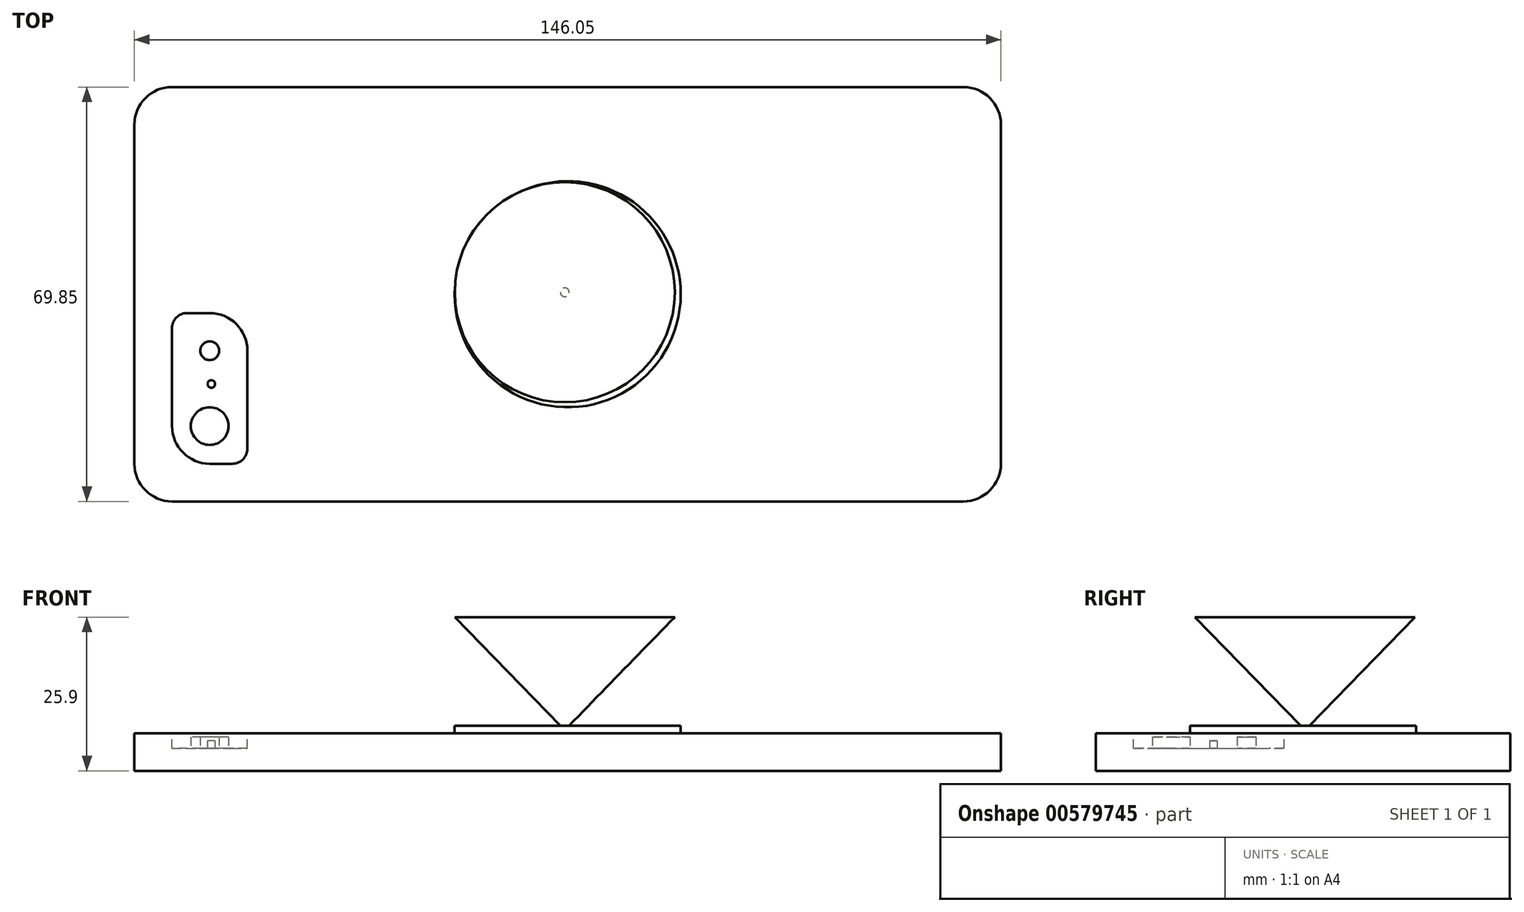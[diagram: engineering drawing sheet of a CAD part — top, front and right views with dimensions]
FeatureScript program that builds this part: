
annotation { "Feature Type Name" : "Feature", "Feature Type Description" : "" }
export const myFeature = defineFeature(function(context is Context, id is Id, definition is map)
    precondition{}
    {
        {
            var Q0;
            Q0=qCreatedBy(makeId("Top.planeOp"),FACE);
            var sketch = newSketch(context, id + "F0", { "sketchPlane" : qUnion([Q0])});
            skLineSegment(sketch, "E0.bottom", {"start": v(-46.88, 61.88) * mm, "end": v(86.47, 61.88) * mm});
            skLineSegment(sketch, "E0.top", {"start": v(-46.88, -7.97) * mm, "end": v(86.47, -7.97) * mm});
            skLineSegment(sketch, "E0.left", {"start": v(-53.23, 55.53) * mm, "end": v(-53.23, -1.62) * mm});
            skLineSegment(sketch, "E0.right", {"start": v(92.82, 55.53) * mm, "end": v(92.82, -1.62) * mm});
            skPoint(sketch, "E1.visualSharp", {"position": v(-53.23, 61.88) * mm});
            skArc(sketch, "E1.filletArc", {"start": v(-46.88, 61.88) * mm, "mid": v(-51.37, 60.02) * mm, "end": v(-53.23, 55.53) * mm});
            skPoint(sketch, "E2.visualSharp", {"position": v(92.82, 61.88) * mm});
            skArc(sketch, "E2.filletArc", {"start": v(92.82, 55.53) * mm, "mid": v(90.96, 60.02) * mm, "end": v(86.47, 61.88) * mm});
            skPoint(sketch, "E3.visualSharp", {"position": v(92.82, -7.97) * mm});
            skArc(sketch, "E3.filletArc", {"start": v(86.47, -7.97) * mm, "mid": v(90.96, -6.1) * mm, "end": v(92.82, -1.62) * mm});
            skPoint(sketch, "E4.visualSharp", {"position": v(-53.23, -7.97) * mm});
            skArc(sketch, "E4.filletArc", {"start": v(-53.23, -1.62) * mm, "mid": v(-51.37, -6.1) * mm, "end": v(-46.88, -7.97) * mm});
            skSolve(sketch);
        }
        {
            var Q0;
            Q0=makeQuery(id+"F0.imprint","IMPRINT",FACE,{"disambiguationData":[TD([[makeQuery(id+"F0.imprint","IMPRINT",EDGE,{"derivedFrom":sQuery(id+"F0.wireOp",EDGE,"E0.bottom")}),-1.0]])]});
            extrude(context, id + "F1", {"entities" : qUnion([Q0]), "depth" : 6.35 * mm, "offsetDistance" : 25.4 * mm});
        }
        {
            var Q0;
            Q0=makeQuery(id+"F1.opExtrude","CAP_FACE",FACE,{"disambiguationData":[OSD([sQuery(id+"F0.wireOp",EDGE,"E0.bottom"),sQuery(id+"F0.wireOp",EDGE,"E0.top"),sQuery(id+"F0.wireOp",EDGE,"E0.left"),sQuery(id+"F0.wireOp",EDGE,"E0.right"),sQuery(id+"F0.wireOp",EDGE,"E1.filletArc"),sQuery(id+"F0.wireOp",EDGE,"E2.filletArc"),sQuery(id+"F0.wireOp",EDGE,"E3.filletArc"),sQuery(id+"F0.wireOp",EDGE,"E4.filletArc")])],"isStart":false});
            var sketch = newSketch(context, id + "F2", { "sketchPlane" : qUnion([Q0])});
            skLineSegment(sketch, "E5.bottom", {"start": v(-40.53, -1.62) * mm, "end": v(-36.72, -1.62) * mm});
            skLineSegment(sketch, "E5.top", {"start": v(-44.34, 23.78) * mm, "end": v(-40.53, 23.78) * mm});
            skLineSegment(sketch, "E5.left", {"start": v(-46.88, 4.73) * mm, "end": v(-46.88, 21.24) * mm});
            skLineSegment(sketch, "E5.right", {"start": v(-34.18, 0.92) * mm, "end": v(-34.18, 17.43) * mm});
            skPoint(sketch, "E6.visualSharp", {"position": v(-46.88, 23.78) * mm});
            skArc(sketch, "E6.filletArc", {"start": v(-44.34, 23.78) * mm, "mid": v(-46.14, 23.04) * mm, "end": v(-46.88, 21.24) * mm});
            skPoint(sketch, "E7.visualSharp", {"position": v(-34.18, -1.62) * mm});
            skArc(sketch, "E7.filletArc", {"start": v(-36.72, -1.62) * mm, "mid": v(-34.93, -0.87) * mm, "end": v(-34.18, 0.92) * mm});
            skPoint(sketch, "E8.visualSharp", {"position": v(-34.18, 23.78) * mm});
            skArc(sketch, "E8.filletArc", {"start": v(-34.18, 17.43) * mm, "mid": v(-36.04, 21.92) * mm, "end": v(-40.53, 23.78) * mm});
            skPoint(sketch, "E9.visualSharp", {"position": v(-46.88, -1.62) * mm});
            skArc(sketch, "E9.filletArc", {"start": v(-46.88, 4.73) * mm, "mid": v(-45.02, 0.24) * mm, "end": v(-40.53, -1.62) * mm});
            skSolve(sketch);
        }
        {
            var Q0;
            Q0=makeQuery(id+"F2.imprint","IMPRINT",FACE,{"disambiguationData":[TD([[makeQuery(id+"F2.imprint","IMPRINT",EDGE,{"derivedFrom":sQuery(id+"F2.wireOp",EDGE,"E5.bottom")}),1.0]])]});
            extrude(context, id + "F3", {"entities" : qUnion([Q0]), "operationType" : NewBodyOperationType.REMOVE, "oppositeDirection" : true, "depth" : 2.54 * mm, "offsetDistance" : 25.4 * mm});
        }
        {
            var Q0;
            Q0=makeQuery(id+"F3.boolean.opBoolean","COPY",FACE,{"derivedFrom":makeQuery(id+"F3.opExtrude","CAP_FACE",FACE,{"disambiguationData":[OSD([sQuery(id+"F2.wireOp",EDGE,"E5.bottom"),sQuery(id+"F2.wireOp",EDGE,"E5.top"),sQuery(id+"F2.wireOp",EDGE,"E5.left"),sQuery(id+"F2.wireOp",EDGE,"E5.right"),sQuery(id+"F2.wireOp",EDGE,"E6.filletArc"),sQuery(id+"F2.wireOp",EDGE,"E7.filletArc"),sQuery(id+"F2.wireOp",EDGE,"E8.filletArc"),sQuery(id+"F2.wireOp",EDGE,"E9.filletArc")])],"isStart":false})});
            var sketch = newSketch(context, id + "F4", { "sketchPlane" : qUnion([Q0])});
            skCircle(sketch, "E10", {"center": v(-40.53, 4.73) * mm, "radius": 3.18 * mm});
            skCircle(sketch, "E11", {"center": v(-40.53, 17.43) * mm, "radius": 1.59 * mm});
            skSolve(sketch);
        }
        {
            var Q0;
            Q0=makeQuery(id+"F4.imprint","IMPRINT",FACE,{"disambiguationData":[TD([[makeQuery(id+"F4.imprint","IMPRINT",EDGE,{"derivedFrom":sQuery(id+"F4.wireOp",EDGE,"E10")}),1.0]])]});
            var Q1;
            Q1=makeQuery(id+"F4.imprint","IMPRINT",FACE,{"disambiguationData":[TD([[makeQuery(id+"F4.imprint","IMPRINT",EDGE,{"derivedFrom":sQuery(id+"F4.wireOp",EDGE,"E11")}),1.0]])]});
            extrude(context, id + "F5", {"entities" : qUnion([Q0, Q1]), "operationType" : NewBodyOperationType.ADD, "depth" : 1.9 * mm, "offsetDistance" : 25.4 * mm});
        }
        {
            var Q0;
            Q0=makeQuery(id+"F3.boolean.opBoolean","COPY",FACE,{"derivedFrom":makeQuery(id+"F3.opExtrude","CAP_FACE",FACE,{"disambiguationData":[OSD([sQuery(id+"F2.wireOp",EDGE,"E5.bottom"),sQuery(id+"F2.wireOp",EDGE,"E5.top"),sQuery(id+"F2.wireOp",EDGE,"E5.left"),sQuery(id+"F2.wireOp",EDGE,"E5.right"),sQuery(id+"F2.wireOp",EDGE,"E6.filletArc"),sQuery(id+"F2.wireOp",EDGE,"E7.filletArc"),sQuery(id+"F2.wireOp",EDGE,"E8.filletArc"),sQuery(id+"F2.wireOp",EDGE,"E9.filletArc")])],"isStart":false})});
            var sketch = newSketch(context, id + "F6", { "sketchPlane" : qUnion([Q0])});
            skCircle(sketch, "E12", {"center": v(-40.26, 11.83) * mm, "radius": 0.64 * mm});
            skSolve(sketch);
        }
        {
            var Q0;
            Q0=makeQuery(id+"F6.imprint","IMPRINT",FACE,{"disambiguationData":[TD([[makeQuery(id+"F6.imprint","IMPRINT",EDGE,{"derivedFrom":sQuery(id+"F6.wireOp",EDGE,"E12")}),1.0]])]});
            extrude(context, id + "F7", {"entities" : qUnion([Q0]), "operationType" : NewBodyOperationType.ADD, "depth" : 1.27 * mm, "offsetDistance" : 25.4 * mm});
        }
        {
            var Q0;
            Q0=makeQuery(id+"F1.opExtrude","CAP_FACE",FACE,{"disambiguationData":[OSD([sQuery(id+"F0.wireOp",EDGE,"E0.bottom"),sQuery(id+"F0.wireOp",EDGE,"E0.top"),sQuery(id+"F0.wireOp",EDGE,"E0.left"),sQuery(id+"F0.wireOp",EDGE,"E0.right"),sQuery(id+"F0.wireOp",EDGE,"E1.filletArc"),sQuery(id+"F0.wireOp",EDGE,"E2.filletArc"),sQuery(id+"F0.wireOp",EDGE,"E3.filletArc"),sQuery(id+"F0.wireOp",EDGE,"E4.filletArc")])],"isStart":false});
            var sketch = newSketch(context, id + "F8", { "sketchPlane" : qUnion([Q0])});
            skPoint(sketch, "E13.startSnap0", {"position": v(92.82, 26.96) * mm});
            skPoint(sketch, "E13.startSnap1", {"position": v(19.8, 61.88) * mm});
            skPoint(sketch, "E13.endSnap0", {"position": v(19.8, -7.97) * mm});
            skCircle(sketch, "E14", {"center": v(19.8, 26.96) * mm, "radius": 19.05 * mm});
            skSolve(sketch);
        }
        {
            var Q0;
            Q0 = qSketchRegion(id + "F8", true);
            extrude(context, id + "F9", {"entities" : qUnion([Q0]), "operationType" : NewBodyOperationType.ADD, "depth" : 1.27 * mm, "offsetDistance" : 25.4 * mm});
        }
        {
            var Q0;
            Q0=qCreatedBy(makeId("Right.planeOp"),FACE);
            cPlane(context, id + "F10", {"entities" : qUnion([Q0]), "cplaneType" : CPlaneType.OFFSET, "offset" : 19.3 * mm, "width" : 152.4 * mm, "height" : 152.4 * mm});
        }
        {
            var Q0;
            Q0=qCreatedBy(id+"F10.planeOp",FACE);
            var sketch = newSketch(context, id + "F11", { "sketchPlane" : qUnion([Q0])});
            skLineSegment(sketch, "E15", {"start": v(27.29, 6.85) * mm, "end": v(27.29, 25.9) * mm});
            skLineSegment(sketch, "E16", {"start": v(27.29, 25.9) * mm, "end": v(45.83, 25.9) * mm});
            skLineSegment(sketch, "E17", {"start": v(45.83, 25.9) * mm, "end": v(27.29, 6.85) * mm});
            skSolve(sketch);
        }
        {
            var Q0;
            Q0=makeQuery(id+"F11.imprint","IMPRINT",FACE,{"disambiguationData":[TD([[makeQuery(id+"F11.imprint","IMPRINT",EDGE,{"derivedFrom":sQuery(id+"F11.wireOp",EDGE,"E15")}),-1.0]])]});
            var Q1;
            Q1=sQuery(id+"F11.wireOp",EDGE,"E15");
            revolve(context, id + "F12", {"operationType" : NewBodyOperationType.ADD, "entities" : qUnion([Q0]), "axis" : qUnion([Q1]), "revolveType" : RevolveType.FULL});
        }
    });
